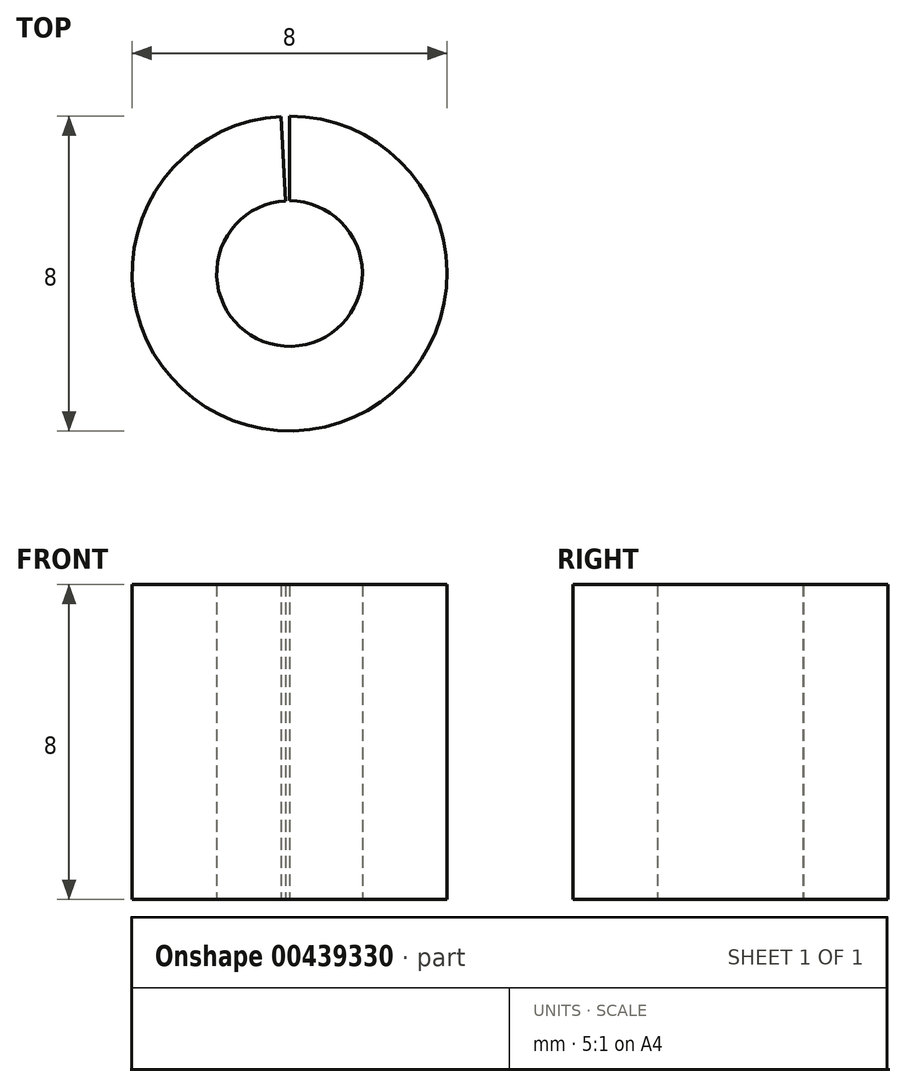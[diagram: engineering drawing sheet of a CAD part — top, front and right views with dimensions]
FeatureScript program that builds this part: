
annotation { "Feature Type Name" : "Feature", "Feature Type Description" : "" }
export const myFeature = defineFeature(function(context is Context, id is Id, definition is map)
    precondition{}
    {
        {
            var Q0;
            Q0=qCreatedBy(makeId("Top.planeOp"),FACE);
            var sketch = newSketch(context, id + "F0", { "sketchPlane" : qUnion([Q0])});
            skArc(sketch, "E0", {"start": v(-0.2, 4) * mm, "mid": v(0.1, -4) * mm, "end": v(0, 4) * mm});
            skArc(sketch, "E1", {"start": v(-0.1, 1.85) * mm, "mid": v(0.05, -1.85) * mm, "end": v(0, 1.85) * mm});
            skLineSegment(sketch, "E2", {"start": v(0, 1.85) * mm, "end": v(0, 4) * mm});
            skLineSegment(sketch, "E3", {"start": v(-0.1, 1.85) * mm, "end": v(-0.2, 4) * mm});
            skSolve(sketch);
        }
        {
            var Q0;
            Q0=makeQuery(id+"F0.imprint","IMPRINT",FACE,{"disambiguationData":[TD([[makeQuery(id+"F0.imprint","IMPRINT",EDGE,{"derivedFrom":sQuery(id+"F0.wireOp",EDGE,"E0")}),1.0]])]});
            extrude(context, id + "F1", {"entities" : qUnion([Q0]), "depth" : 8 * mm});
        }
    });
